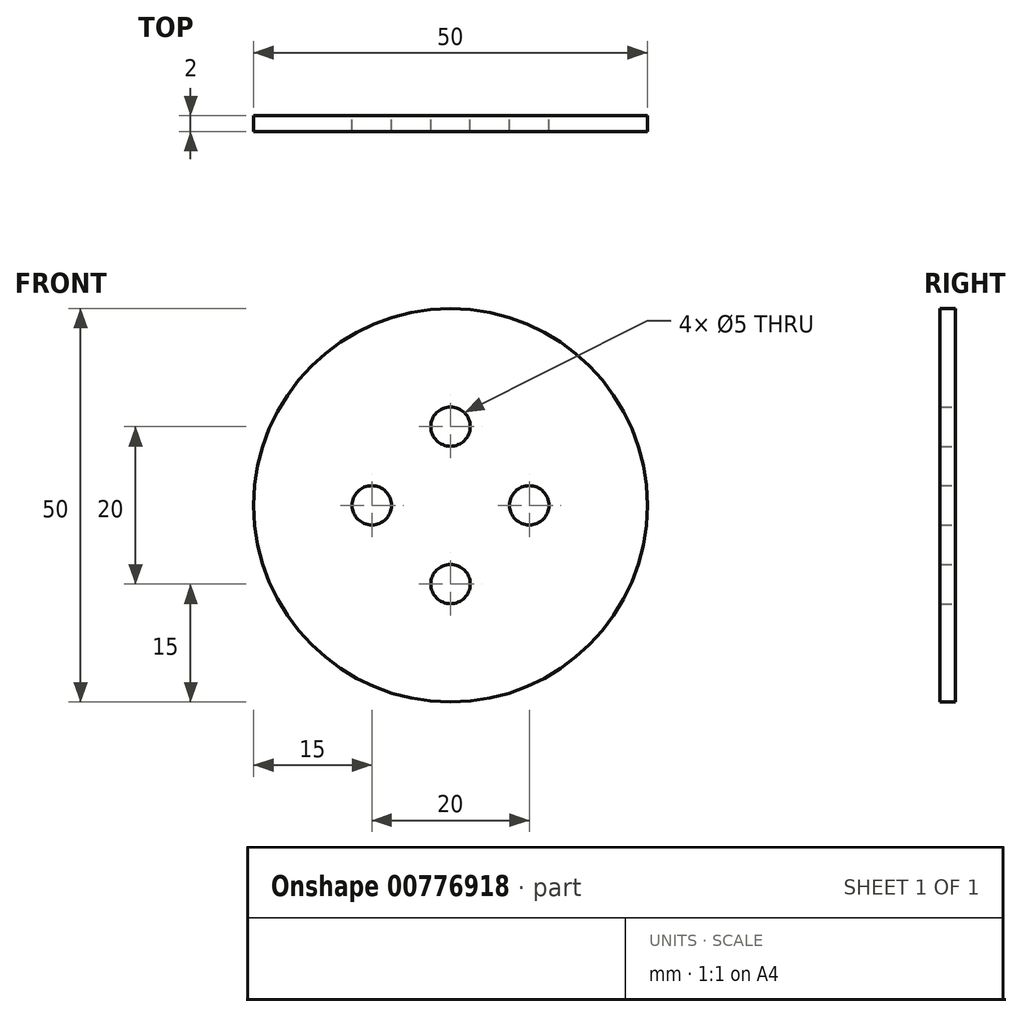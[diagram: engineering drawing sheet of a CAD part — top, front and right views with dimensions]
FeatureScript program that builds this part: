
annotation { "Feature Type Name" : "Feature", "Feature Type Description" : "" }
export const myFeature = defineFeature(function(context is Context, id is Id, definition is map)
    precondition{}
    {
        {
            var Q0;
            Q0=qCreatedBy(makeId("Front.planeOp"),FACE);
            var sketch = newSketch(context, id + "F0", { "sketchPlane" : qUnion([Q0])});
            skCircle(sketch, "E0", {"center": v(0, 0) * mm, "radius": 25 * mm});
            skSolve(sketch);
        }
        {
            var Q0;
            Q0=makeQuery(id+"F0.imprint","IMPRINT",FACE,{"disambiguationData":[TD([[makeQuery(id+"F0.imprint","IMPRINT",EDGE,{"derivedFrom":sQuery(id+"F0.wireOp",EDGE,"E0")}),1.0]])]});
            var sketch = newSketch(context, id + "F1", { "sketchPlane" : qUnion([Q0])});
            skCircle(sketch, "E1", {"center": v(0, 0) * mm, "radius": 10 * mm, "construction": true});
            skCircle(sketch, "E2", {"center": v(0, 10) * mm, "radius": 2.02 * mm});
            skSolve(sketch);
        }
        {
            var Q0;
            Q0=makeQuery(id+"F0.imprint","IMPRINT",FACE,{"disambiguationData":[TD([[makeQuery(id+"F0.imprint","IMPRINT",EDGE,{"derivedFrom":sQuery(id+"F0.wireOp",EDGE,"E0")}),1.0]])]});
            extrude(context, id + "F2", {"entities" : qUnion([Q0]), "depth" : 2 * mm, "offsetDistance" : 25 * mm});
        }
        {
            var Q0;
            Q0=sQuery(id+"F1.wireOp",VERTEX,"E2.center");
            var Q1;
            Q1=makeQuery(id+"F2.opExtrude","SWEPT_BODY",BODY,{"disambiguationData":[OSD([sQuery(id+"F0.wireOp",EDGE,"E0")])]});
            hole(context, id + "F3", {"style" : HoleStyle.SIMPLE, "endStyle" : HoleEndStyle.THROUGH, "oppositeDirection" : true, "holeDiameter" : 5 * mm, "majorDiameter" : 5 * mm, "isTappedThrough" : true, "tappedDepth" : 12 * mm, "tapClearance" : 3, "locations" : qUnion([Q0]), "scope" : qUnion([Q1])});
        }
        {
            var Q0;
            Q0=makeQuery(id+"F2.opExtrude","SWEPT_BODY",BODY,{"disambiguationData":[OSD([sQuery(id+"F0.wireOp",EDGE,"E0")])]});
            var Q1;
            Q1=sQuery(id+"F1.wireOp",EDGE,"E1");
            circularPattern(context, id + "F4", {"entities" : qUnion([Q0]), "axis" : qUnion([Q1]), "angle" : 360 * degree, "instanceCount" : 4, "equalSpace" : true});
        }
    });
